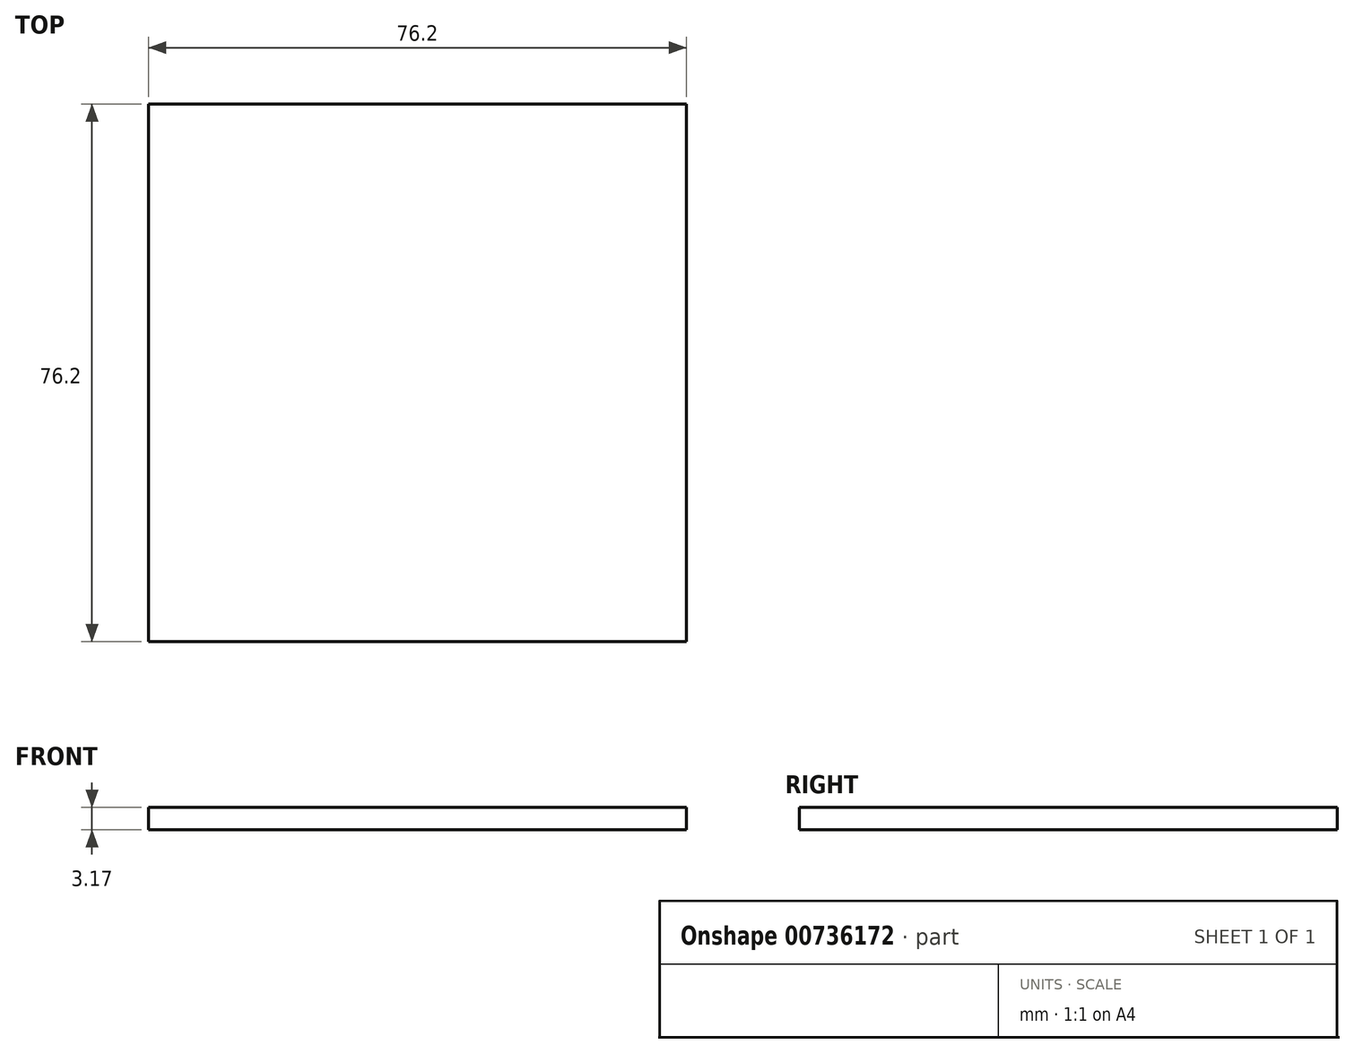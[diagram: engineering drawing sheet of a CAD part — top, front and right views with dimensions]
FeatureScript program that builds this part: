
annotation { "Feature Type Name" : "Feature", "Feature Type Description" : "" }
export const myFeature = defineFeature(function(context is Context, id is Id, definition is map)
    precondition{}
    {
        {
            var Q0;
            Q0=qCreatedBy(makeId("Top.planeOp"),FACE);
            var sketch = newSketch(context, id + "F0", { "sketchPlane" : qUnion([Q0])});
            skLineSegment(sketch, "E0.bottom", {"start": v(-40.2, -39.05) * mm, "end": v(36, -39.05) * mm});
            skLineSegment(sketch, "E0.top", {"start": v(-40.2, 37.15) * mm, "end": v(36, 37.15) * mm});
            skLineSegment(sketch, "E0.left", {"start": v(-40.2, -39.05) * mm, "end": v(-40.2, 37.15) * mm});
            skLineSegment(sketch, "E0.right", {"start": v(36, -39.05) * mm, "end": v(36, 37.15) * mm});
            skLineSegment(sketch, "E1.bottom", {"start": v(-40.2, 37.15) * mm, "end": v(-33.85, 37.15) * mm});
            skLineSegment(sketch, "E1.left", {"start": v(-40.2, 37.15) * mm, "end": v(-40.2, 30.8) * mm});
            skLineSegment(sketch, "E2.bottom", {"start": v(36, 37.15) * mm, "end": v(29.65, 37.15) * mm});
            skLineSegment(sketch, "E2.left", {"start": v(36, 37.15) * mm, "end": v(36, 30.8) * mm});
            skLineSegment(sketch, "E3.bottom", {"start": v(-40.2, -39.05) * mm, "end": v(-33.85, -39.05) * mm});
            skLineSegment(sketch, "E3.left", {"start": v(-40.2, -39.05) * mm, "end": v(-40.2, -32.7) * mm});
            skLineSegment(sketch, "E4.bottom", {"start": v(36, -39.05) * mm, "end": v(29.65, -39.05) * mm});
            skLineSegment(sketch, "E4.left", {"start": v(36, -39.05) * mm, "end": v(36, -32.7) * mm});
            skSolve(sketch);
        }
        {
            var Q0;
            Q0=makeQuery(id+"F0.imprint","IMPRINT",FACE,{"disambiguationData":[TD([[makeQuery(id+"F0.imprint","IMPRINT",EDGE,{"derivedFrom":sQuery(id+"F0.wireOp",EDGE,"E0.bottom")}),1.0]])]});
            extrude(context, id + "F1", {"entities" : qUnion([Q0]), "depth" : 3.17 * mm, "offsetDistance" : 25.4 * mm});
        }
    });
